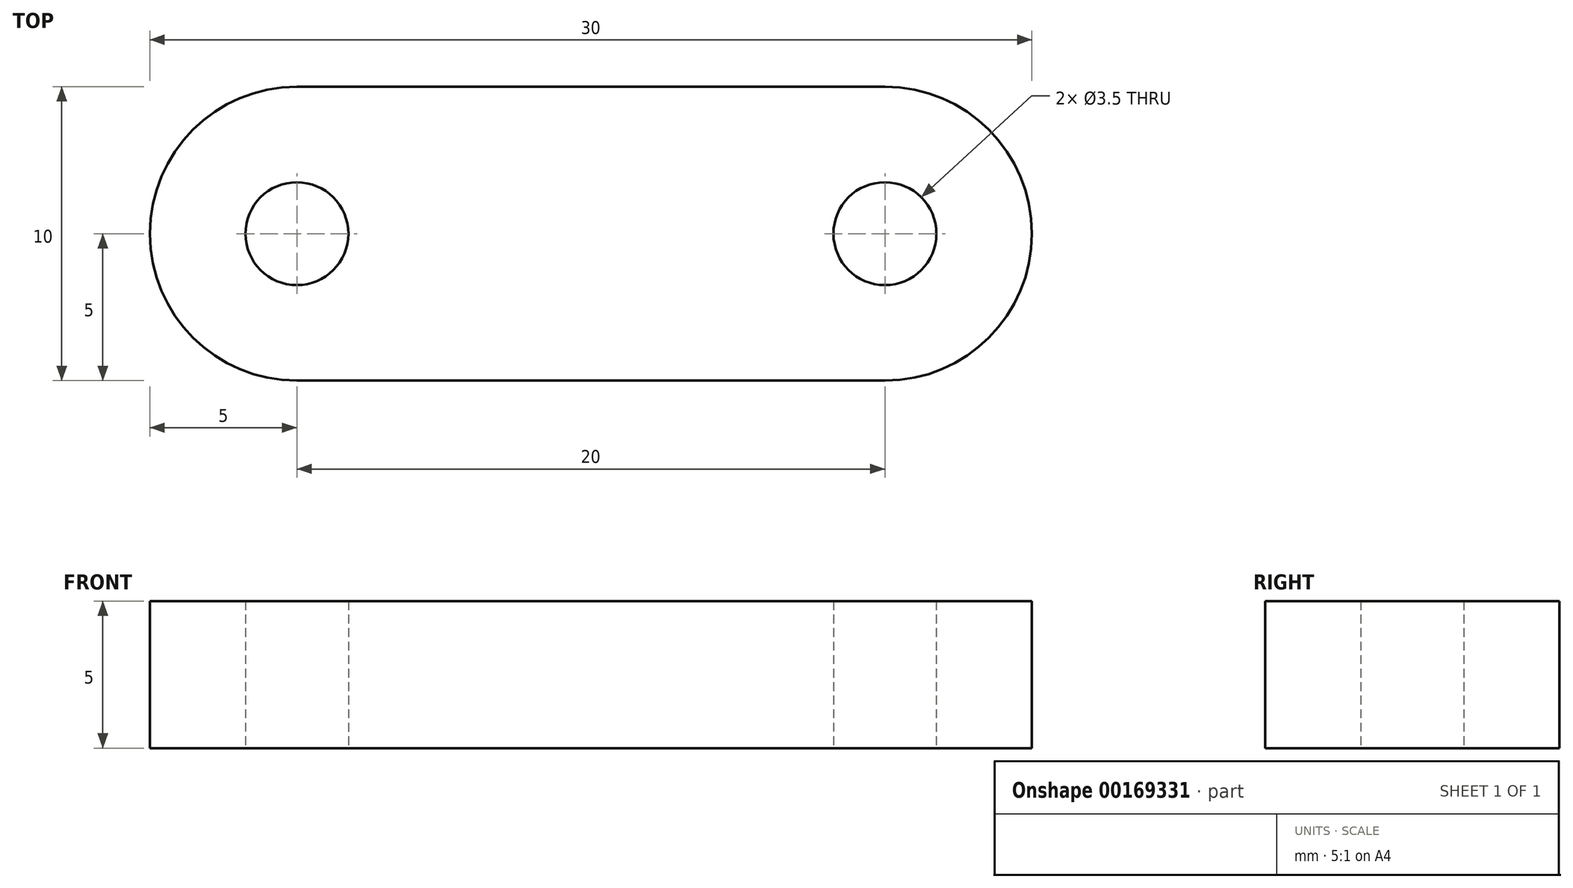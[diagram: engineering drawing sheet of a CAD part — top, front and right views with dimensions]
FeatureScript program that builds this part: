
annotation { "Feature Type Name" : "Feature", "Feature Type Description" : "" }
export const myFeature = defineFeature(function(context is Context, id is Id, definition is map)
    precondition{}
    {
        {
            var Q0;
            Q0=qCreatedBy(makeId("Top.planeOp"),FACE);
            var sketch = newSketch(context, id + "F0", { "sketchPlane" : qUnion([Q0])});
            skLineSegment(sketch, "E0.bottom", {"start": v(10, -5) * mm, "end": v(-10, -5) * mm});
            skLineSegment(sketch, "E0.top", {"start": v(10, 5) * mm, "end": v(-10, 5) * mm});
            skLineSegment(sketch, "E0.left", {"start": v(15, 0) * mm, "end": v(15, 0) * mm});
            skLineSegment(sketch, "E0.right", {"start": v(-15, 0) * mm, "end": v(-15, 0) * mm});
            skPoint(sketch, "E0.middle", {"position": v(0, 0) * mm});
            skCircle(sketch, "E1", {"center": v(-10, 0) * mm, "radius": 1.75 * mm});
            skCircle(sketch, "E2", {"center": v(10, 0) * mm, "radius": 1.75 * mm});
            skPoint(sketch, "E3.visualSharp", {"position": v(-15, 5) * mm});
            skArc(sketch, "E3.filletArc", {"start": v(-10, 5) * mm, "mid": v(-13.54, 3.54) * mm, "end": v(-15, 0) * mm});
            skPoint(sketch, "E4.visualSharp", {"position": v(-15, -5) * mm});
            skArc(sketch, "E4.filletArc", {"start": v(-15, 0) * mm, "mid": v(-13.54, -3.54) * mm, "end": v(-10, -5) * mm});
            skPoint(sketch, "E5.visualSharp", {"position": v(15, -5) * mm});
            skArc(sketch, "E5.filletArc", {"start": v(10, -5) * mm, "mid": v(13.54, -3.54) * mm, "end": v(15, 0) * mm});
            skPoint(sketch, "E6.visualSharp", {"position": v(15, 5) * mm});
            skArc(sketch, "E6.filletArc", {"start": v(15, 0) * mm, "mid": v(13.54, 3.54) * mm, "end": v(10, 5) * mm});
            skSolve(sketch);
        }
        {
            var Q0;
            Q0=makeQuery(id+"F0.imprint","IMPRINT",FACE,{"disambiguationData":[TD([[makeQuery(id+"F0.imprint","IMPRINT",EDGE,{"derivedFrom":sQuery(id+"F0.wireOp",EDGE,"E0.bottom")}),-1.0]])]});
            extrude(context, id + "F1", {"entities" : qUnion([Q0]), "depth" : 5 * mm});
        }
    });
